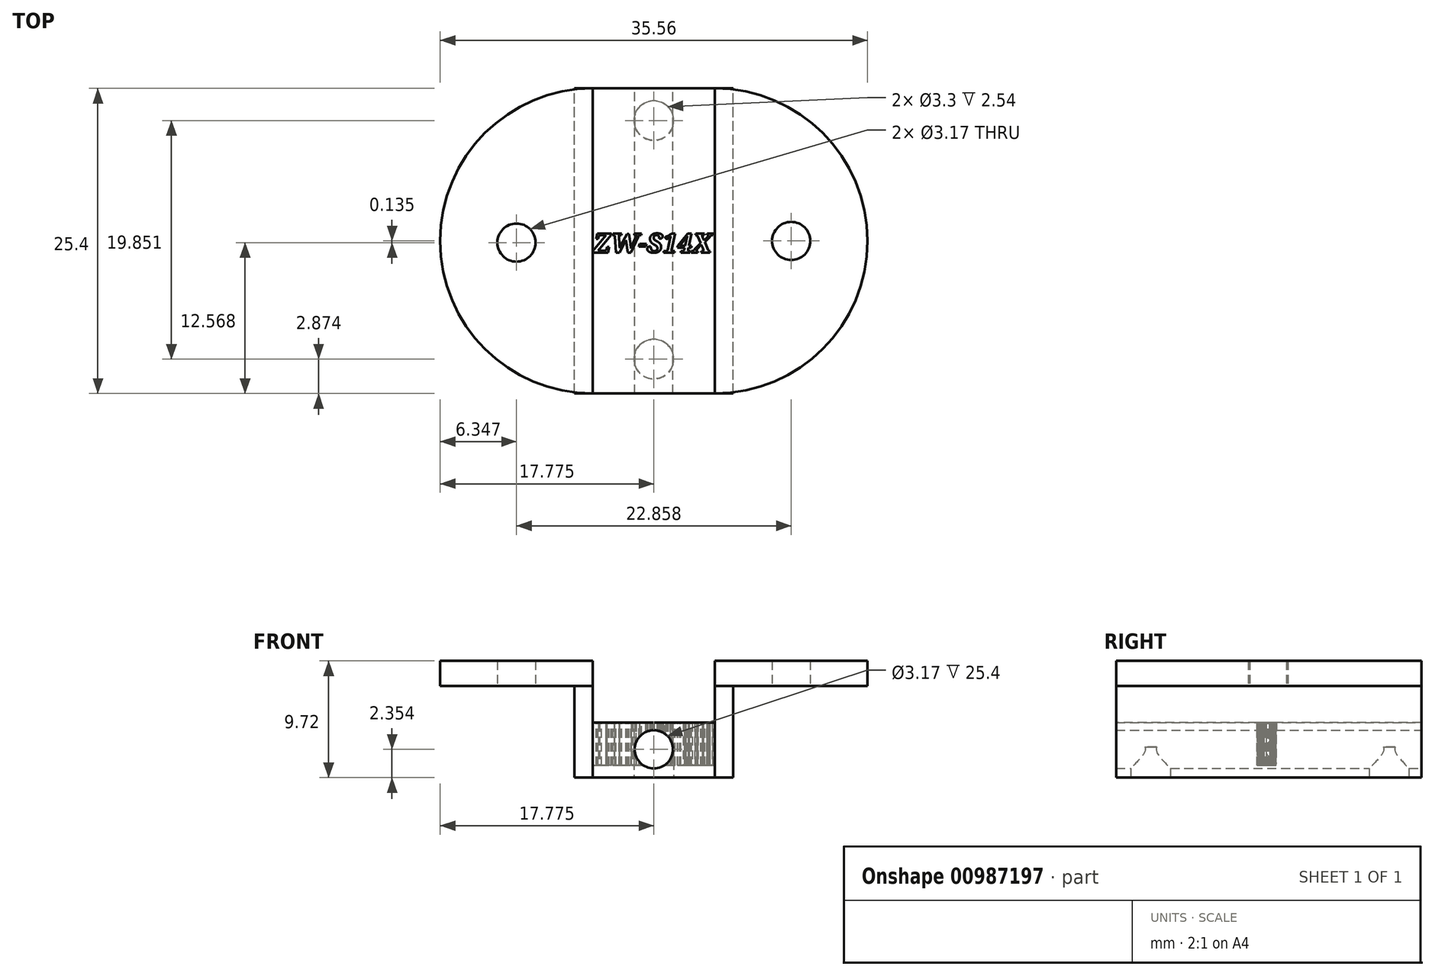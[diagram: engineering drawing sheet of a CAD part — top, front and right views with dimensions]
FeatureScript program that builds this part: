
annotation { "Feature Type Name" : "Feature", "Feature Type Description" : "" }
export const myFeature = defineFeature(function(context is Context, id is Id, definition is map)
    precondition{}
    {
        {
            var Q0;
            Q0=qCreatedBy(makeId("Top.planeOp"),FACE);
            var sketch = newSketch(context, id + "F0", { "sketchPlane" : qUnion([Q0])});
            skLineSegment(sketch, "E0", {"start": v(-48.3, 33.5) * mm, "end": v(-48.3, 8.1) * mm});
            skLineSegment(sketch, "E1", {"start": v(-48.3, 8.1) * mm, "end": v(-48.3, 33.5) * mm});
            skLineSegment(sketch, "E2", {"start": v(-48.3, 33.5) * mm, "end": v(-38.13, 33.5) * mm});
            skLineSegment(sketch, "E3", {"start": v(-38.13, 8.1) * mm, "end": v(-48.3, 8.1) * mm});
            skLineSegment(sketch, "E4", {"start": v(-38.13, 8.1) * mm, "end": v(-38.13, 33.5) * mm});
            skLineSegment(sketch, "E5.bottom", {"start": v(-38.13, 33.5) * mm, "end": v(-36.61, 33.5) * mm});
            skLineSegment(sketch, "E5.top", {"start": v(-38.13, 33.5) * mm, "end": v(-36.61, 33.5) * mm});
            skLineSegment(sketch, "E5.left", {"start": v(-38.13, 33.5) * mm, "end": v(-38.13, 33.5) * mm});
            skLineSegment(sketch, "E5.right", {"start": v(-36.61, 33.5) * mm, "end": v(-36.61, 33.5) * mm});
            skLineSegment(sketch, "E6.bottom", {"start": v(-38.13, 8.1) * mm, "end": v(-36.61, 8.1) * mm});
            skLineSegment(sketch, "E7", {"start": v(-48.3, 33.5) * mm, "end": v(-49.82, 33.5) * mm});
            skLineSegment(sketch, "E8", {"start": v(-48.3, 8.1) * mm, "end": v(-49.82, 8.1) * mm});
            skLineSegment(sketch, "E9", {"start": v(-49.82, 8.1) * mm, "end": v(-49.82, 33.5) * mm});
            skLineSegment(sketch, "E10", {"start": v(-36.61, 8.1) * mm, "end": v(-36.61, 33.5) * mm});
            skLineSegment(sketch, "E11.bottom", {"start": v(-36.61, 8.1) * mm, "end": v(-38.13, 8.1) * mm});
            skLineSegment(sketch, "E11.top", {"start": v(-36.61, 33.5) * mm, "end": v(-38.13, 33.5) * mm});
            skLineSegment(sketch, "E12.bottom", {"start": v(-48.3, 8.1) * mm, "end": v(-38.03, 8.1) * mm});
            skLineSegment(sketch, "E13.bottom", {"start": v(-36.61, 33.5) * mm, "end": v(-21.77, 33.5) * mm});
            skLineSegment(sketch, "E13.top", {"start": v(-36.61, 33.5) * mm, "end": v(-21.77, 33.5) * mm});
            skLineSegment(sketch, "E13.right", {"start": v(-21.77, 33.5) * mm, "end": v(-21.77, 33.5) * mm});
            skLineSegment(sketch, "E14.bottom", {"start": v(-36.61, 8.1) * mm, "end": v(-21.77, 8.1) * mm});
            skLineSegment(sketch, "E14.top", {"start": v(-36.61, 8.1) * mm, "end": v(-21.77, 8.1) * mm});
            skLineSegment(sketch, "E14.left", {"start": v(-36.61, 8.1) * mm, "end": v(-36.61, 8.1) * mm});
            skLineSegment(sketch, "E14.right", {"start": v(-21.77, 8.1) * mm, "end": v(-21.77, 8.1) * mm});
            skLineSegment(sketch, "E15.bottom", {"start": v(-49.82, 8.1) * mm, "end": v(-64.66, 8.1) * mm});
            skLineSegment(sketch, "E15.top", {"start": v(-49.82, 8.1) * mm, "end": v(-64.66, 8.1) * mm});
            skLineSegment(sketch, "E15.left", {"start": v(-49.82, 8.1) * mm, "end": v(-49.82, 8.1) * mm});
            skLineSegment(sketch, "E15.right", {"start": v(-64.66, 8.1) * mm, "end": v(-64.66, 8.1) * mm});
            skLineSegment(sketch, "E16.bottom", {"start": v(-49.82, 33.5) * mm, "end": v(-64.66, 33.5) * mm});
            skLineSegment(sketch, "E16.top", {"start": v(-49.82, 33.5) * mm, "end": v(-64.66, 33.5) * mm});
            skLineSegment(sketch, "E16.left", {"start": v(-49.82, 33.5) * mm, "end": v(-49.82, 33.5) * mm});
            skLineSegment(sketch, "E16.right", {"start": v(-64.66, 33.5) * mm, "end": v(-64.66, 33.5) * mm});
            skLineSegment(sketch, "E17", {"start": v(-64.66, 33.5) * mm, "end": v(-64.66, 8.1) * mm});
            skLineSegment(sketch, "E18", {"start": v(-21.77, 33.5) * mm, "end": v(-21.77, 8.1) * mm});
            skSolve(sketch);
        }
        {
            var Q0;
            Q0=qCreatedBy(makeId("Front.planeOp"),FACE);
            var sketch = newSketch(context, id + "F1", { "sketchPlane" : qUnion([Q0])});
            skSolve(sketch);
        }
        {
            var Q0;
            Q0=makeQuery(id+"F0.imprint","IMPRINT",FACE,{"disambiguationData":[TD([[makeQuery(id+"F0.imprint","IMPRINT",EDGE,{"derivedFrom":sQuery(id+"F0.wireOp",EDGE,"E0")}),1.0]])]});
            extrude(context, id + "F2", {"entities" : qUnion([Q0]), "depth" : 4.57 * mm, "offsetDistance" : 25.4 * mm});
        }
        {
            var Q0;
            Q0=qSketchRegion(id+"F1",true);
            var Q1;
            {var subQ1=sQuery(id+"F0.wireOp",EDGE,"E4");Q1=makeQuery(id+"F0.imprint","IMPRINT",FACE,{"disambiguationData":[TD([[makeQuery(id+"F0.imprint","IMPRINT",EDGE,{"derivedFrom":subQ1}),-1.0]])]});}
            var Q2;
            Q2=makeQuery(id+"F0.imprint","IMPRINT",FACE,{"disambiguationData":[TD([[makeQuery(id+"F0.imprint","IMPRINT",EDGE,{"derivedFrom":sQuery(id+"F0.wireOp",EDGE,"E0")}),-1.0]])]});
            extrude(context, id + "F3", {"entities" : qUnion([Q0, Q1, Q2]), "depth" : 7.62 * mm, "offsetDistance" : 25.4 * mm});
        }
        {
            var Q0;
            Q0=makeQuery(id+"F3.opExtrude","CAP_FACE",FACE,{"disambiguationData":[OSD([sQuery(id+"F0.wireOp",EDGE,"E0"),sQuery(id+"F0.wireOp",EDGE,"E7"),sQuery(id+"F0.wireOp",EDGE,"E8"),sQuery(id+"F0.wireOp",EDGE,"E9")])],"isStart":false});
            var sketch = newSketch(context, id + "F4", { "sketchPlane" : qUnion([Q0])});
            skArc(sketch, "E19", {"start": v(-48.3, 33.5) * mm, "mid": v(-61, 20.8) * mm, "end": v(-48.3, 8.1) * mm});
            skCircle(sketch, "E20", {"center": v(-54.64, 20.67) * mm, "radius": 1.59 * mm});
            skPoint(sketch, "E20.centerSnap0", {"position": v(-59.55, 20.67) * mm});
            skSolve(sketch);
        }
        {
            var Q0;
            Q0=makeQuery(id+"F3.opExtrude","CAP_FACE",FACE,{"disambiguationData":[OSD([sQuery(id+"F0.wireOp",EDGE,"E4"),sQuery(id+"F0.wireOp",EDGE,"E5.bottom"),sQuery(id+"F0.wireOp",EDGE,"E6.bottom"),sQuery(id+"F0.wireOp",EDGE,"E10")])],"isStart":false});
            var sketch = newSketch(context, id + "F5", { "sketchPlane" : qUnion([Q0])});
            skArc(sketch, "E21", {"start": v(-38.13, 8.1) * mm, "mid": v(-25.43, 20.8) * mm, "end": v(-38.13, 33.5) * mm});
            skCircle(sketch, "E22", {"center": v(-31.78, 20.8) * mm, "radius": 1.59 * mm});
            skPoint(sketch, "E22.centerSnap0", {"position": v(-25.43, 20.8) * mm});
            skSolve(sketch);
        }
        {
            var Q0;
            Q0=makeQuery(id+"F4.imprint","IMPRINT",FACE,{"disambiguationData":[TD([[makeQuery(id+"F4.imprint","IMPRINT",EDGE,{"derivedFrom":sQuery(id+"F4.wireOp",EDGE,"E19")}),1.0]])]});
            var Q1;
            Q1=makeQuery(id+"F4.imprint","IMPRINT",FACE,{"disambiguationData":[TD([[makeQuery(id+"F4.imprint","IMPRINT",EDGE,{"derivedFrom":sQuery(id+"F4.wireOp",EDGE,"E20")}),-1.0]])]});
            extrude(context, id + "F6", {"entities" : qUnion([Q0, Q1]), "depth" : 2.1 * mm, "offsetDistance" : 25.4 * mm});
        }
        {
            var Q0;
            Q0=makeQuery(id+"F5.imprint","IMPRINT",FACE,{"disambiguationData":[TD([[makeQuery(id+"F5.imprint","IMPRINT",EDGE,{"derivedFrom":sQuery(id+"F5.wireOp",EDGE,"E21")}),1.0]])]});
            var Q1;
            Q1=makeQuery(id+"F5.imprint","IMPRINT",FACE,{"disambiguationData":[TD([[makeQuery(id+"F5.imprint","IMPRINT",EDGE,{"derivedFrom":sQuery(id+"F5.wireOp",EDGE,"E22")}),-1.0]])]});
            extrude(context, id + "F7", {"entities" : qUnion([Q0, Q1]), "depth" : 2.1 * mm, "offsetDistance" : 25.4 * mm});
        }
        {
            var Q0;
            Q0=makeQuery(id+"F2.opExtrude","SWEPT_FACE",FACE,{"disambiguationData":[OSD([sQuery(id+"F0.wireOp",EDGE,"E2")])]});
            var sketch = newSketch(context, id + "F8", { "sketchPlane" : qUnion([Q0])});
            skCircle(sketch, "E23", {"center": v(43.21, 2.35) * mm, "radius": 1.59 * mm});
            skSolve(sketch);
        }
        {
            var Q0;
            Q0=makeQuery(id+"F8.imprint","IMPRINT",FACE,{"disambiguationData":[TD([[makeQuery(id+"F8.imprint","IMPRINT",EDGE,{"derivedFrom":sQuery(id+"F8.wireOp",EDGE,"E23")}),1.0]])]});
            extrude(context, id + "F9", {"entities" : qUnion([Q0]), "operationType" : NewBodyOperationType.REMOVE, "oppositeDirection" : true, "depth" : 25.4 * mm, "offsetDistance" : 25.4 * mm});
        }
        {
            var Q0;
            Q0=makeQuery(id+"F2.opExtrude","CAP_FACE",FACE,{"disambiguationData":[OSD([sQuery(id+"F0.wireOp",EDGE,"E0"),sQuery(id+"F0.wireOp",EDGE,"E2"),sQuery(id+"F0.wireOp",EDGE,"E3"),sQuery(id+"F0.wireOp",EDGE,"E4")])],"isStart":true});
            var sketch = newSketch(context, id + "F10", { "sketchPlane" : qUnion([Q0])});
            skCircle(sketch, "E24", {"center": v(-43.21, -10.97) * mm, "radius": 1.65 * mm});
            skPoint(sketch, "E24.centerSnap0", {"position": v(-43.21, -8.1) * mm});
            skCircle(sketch, "E25", {"center": v(-43.21, -30.82) * mm, "radius": 1.65 * mm});
            skPoint(sketch, "E25.centerSnap0", {"position": v(-43.21, -33.5) * mm});
            skLineSegment(sketch, "E26", {"start": v(-43.21, -8.1) * mm, "end": v(-43.21, -10.97) * mm, "construction": true});
            skLineSegment(sketch, "E27", {"start": v(-43.21, -33.5) * mm, "end": v(-43.21, -30.82) * mm, "construction": true});
            skSolve(sketch);
        }
        {
            var Q0;
            Q0=makeQuery(id+"F10.imprint","IMPRINT",FACE,{"disambiguationData":[TD([[makeQuery(id+"F10.imprint","IMPRINT",EDGE,{"derivedFrom":sQuery(id+"F10.wireOp",EDGE,"E25")}),1.0]])]});
            var Q1;
            Q1=makeQuery(id+"F10.imprint","IMPRINT",FACE,{"disambiguationData":[TD([[makeQuery(id+"F10.imprint","IMPRINT",EDGE,{"derivedFrom":sQuery(id+"F10.wireOp",EDGE,"E24")}),1.0]])]});
            extrude(context, id + "F11", {"entities" : qUnion([Q0, Q1]), "operationType" : NewBodyOperationType.REMOVE, "oppositeDirection" : true, "depth" : 2.54 * mm, "offsetDistance" : 25.4 * mm});
        }
        {
            var Q0;
            Q0=makeQuery(id+"F2.opExtrude","CAP_FACE",FACE,{"disambiguationData":[OSD([sQuery(id+"F0.wireOp",EDGE,"E0"),sQuery(id+"F0.wireOp",EDGE,"E2"),sQuery(id+"F0.wireOp",EDGE,"E3"),sQuery(id+"F0.wireOp",EDGE,"E4")])],"isStart":false});
            var sketch = newSketch(context, id + "F12", { "sketchPlane" : qUnion([Q0])});
            skText(sketch, "E28", { "text": "ZW-S14X", "fontName": "NotoSerif-BoldItalic.ttf"});
            const initialGuessF12  = {"E28": [-0.0483, 0.01984, 1, 0, 0.00159]};
            skSetInitialGuess(sketch, initialGuessF12);
            skSolve(sketch);
        }
        {
            var Q0;
            Q0 = qSketchRegion(id + "F12", true);
            extrude(context, id + "F13", {"entities" : qUnion([Q0]), "operationType" : NewBodyOperationType.REMOVE, "oppositeDirection" : true, "depth" : 3.56 * mm, "offsetDistance" : 25.4 * mm});
        }
    });
